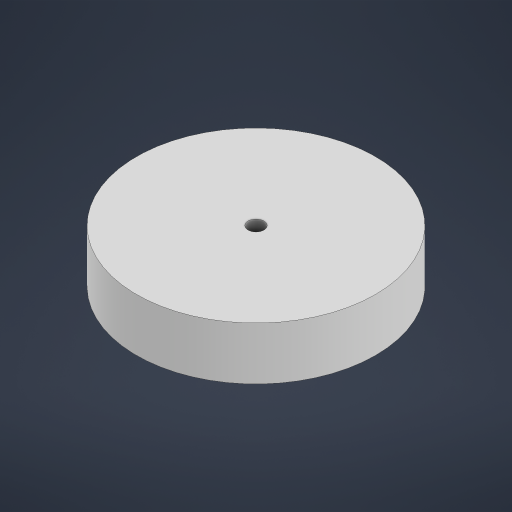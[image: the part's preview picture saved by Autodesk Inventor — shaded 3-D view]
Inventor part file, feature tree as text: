
AUTODESK INVENTOR PART (.ipt)
format: ipt  version: 2024 (Build 280153000, 153)  size: 154,624 bytes
history: native  units: mm
features: other x1, extrude x1, sketch x1
ambient origin geometry x8: Origin, YZ Plane, XZ Plane, XY Plane, X Axis, Y Axis, Z Axis, Center Point
bodies: Body1 (feature_tree)
feature tree (3):
  other  "Твердое тело1"
  extrude  "Выдавливание1"  Depth=8.0mm
  sketch  "Эскиз1"
